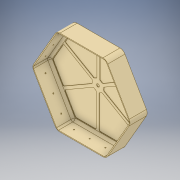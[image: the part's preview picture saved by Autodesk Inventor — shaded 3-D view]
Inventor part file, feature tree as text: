
AUTODESK INVENTOR PART (.ipt)
format: ipt  version: 2019 (Build 230136000, 136)  size: 606,208 bytes
history: native  units: mm
features: mirror x4, extrude x3, sketch x3, plane x3, fillet x3, projected_geometry x2, shell x1
ambient origin geometry x8: Origin, YZ Plane, XZ Plane, XY Plane, X Axis, Y Axis, Z Axis, Center Point
bodies: Solid1 (feature_tree)
feature tree (19):
  extrude  "Extrusion1"  Depth=30.0mm TaperAngle=0.0deg
  shell  "Shell1"  Thickness=1.5mm
  sketch  "Sketch2"  dims[d5=2.0mm d6=15.0mm]
  plane  "Work Plane1"
  plane  "Work Plane2"
  plane  "Work Plane3"
  extrude  "Extrusion5"  Depth=2.0mm
  extrude  "Extrusion2"  Depth=1.0mm TaperAngle=0.0deg
  mirror  "Mirror1"
  mirror  "Mirror2"
  mirror  "Mirror3"
  mirror  "Mirror4"
  fillet  "Fillet1"  Radius=4.0mm
  fillet  "Fillet2"  Radius=10.0mm
  fillet  "Fillet4"  Radius=1.0mm
  sketch  "Sketch1"  dims[d0=150.0mm d2=30.0mm d3=0.0mm d4=1.5mm]
  projected_geometry  "Projected Loop1"
  sketch  "Sketch4"  dims[d7=15.0mm d8=1.0mm d9=0.0mm d10=4.0mm d11=10.0mm d12=1.0mm d37=5.0mm d44=10.0mm d45=60.0deg d46=90.0deg d47=90.0deg d48=60.0mm d50=360.0deg d52=5.5mm d53=0.75mm d54=0.0mm d55=5.0mm d56=2.0mm]
  projected_geometry  "Projected Loop3"
